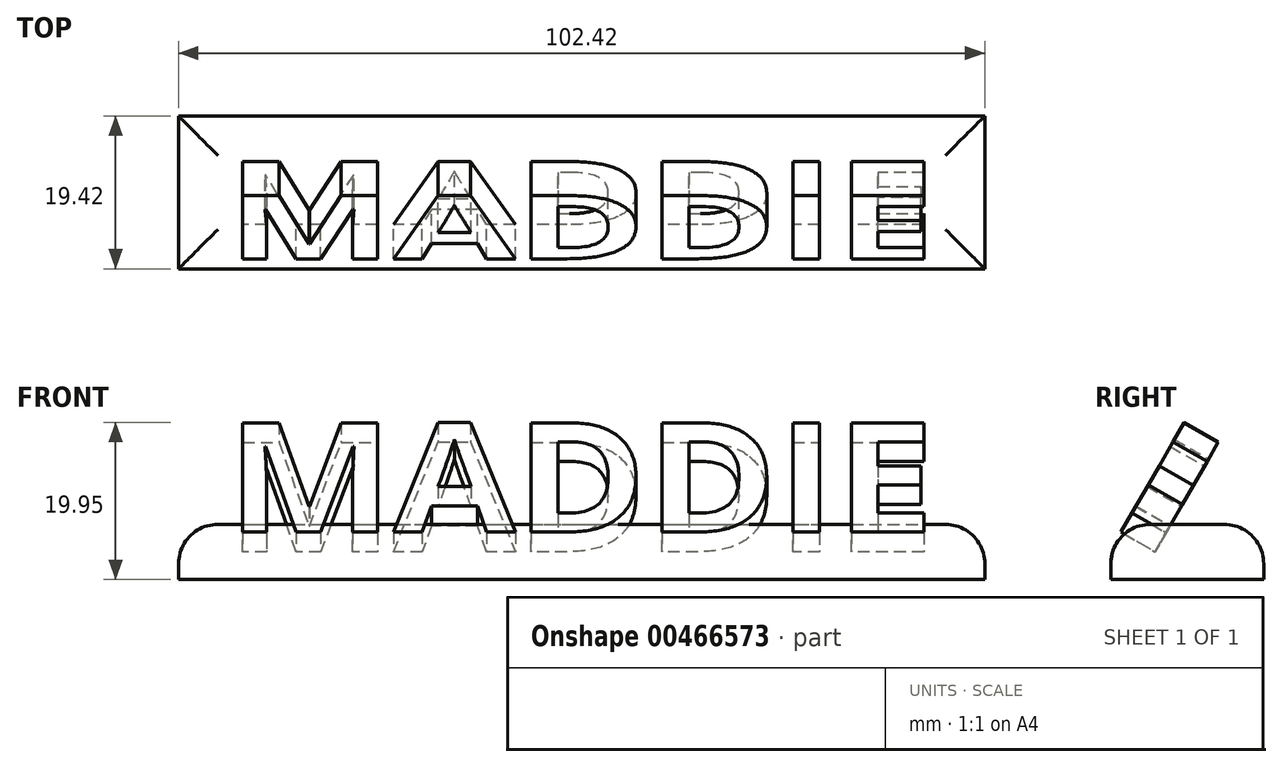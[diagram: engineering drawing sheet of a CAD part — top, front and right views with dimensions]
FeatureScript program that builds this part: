
annotation { "Feature Type Name" : "Feature", "Feature Type Description" : "" }
export const myFeature = defineFeature(function(context is Context, id is Id, definition is map)
    precondition{}
    {
        {
            var Q0;
            Q0=qCreatedBy(makeId("Top.planeOp"),FACE);
            var sketch = newSketch(context, id + "F0", { "sketchPlane" : qUnion([Q0])});
            skText(sketch, "E0", { "text": "MADDIE", "fontName": "OpenSans-Bold.ttf"});
            const initialGuessF0  = {"E0": [-0.03343, -0.00687, 1, 0, 0.01616]};
            skSetInitialGuess(sketch, initialGuessF0);
            skSolve(sketch);
        }
        {
            var Q0;
            Q0=qSketchRegion(id+"F0",true);
            extrude(context, id + "F1", {"entities" : qUnion([Q0]), "depth" : 5 * mm});
        }
        {
            var Q0;
            Q0=qCreatedBy(makeId("Top.planeOp"),FACE);
            var sketch = newSketch(context, id + "F2", { "sketchPlane" : qUnion([Q0])});
            skLineSegment(sketch, "E1.bottom", {"start": v(-39.57, 31.58) * mm, "end": v(62.85, 31.58) * mm});
            skLineSegment(sketch, "E1.top", {"start": v(-39.57, 12.16) * mm, "end": v(62.85, 12.16) * mm});
            skLineSegment(sketch, "E1.left", {"start": v(-39.57, 31.58) * mm, "end": v(-39.57, 12.16) * mm});
            skLineSegment(sketch, "E1.right", {"start": v(62.85, 31.58) * mm, "end": v(62.85, 12.16) * mm});
            skSolve(sketch);
        }
        {
            var Q0;
            Q0=makeQuery(id+"F2.imprint","IMPRINT",FACE,{"disambiguationData":[TD([[makeQuery(id+"F2.imprint","IMPRINT",EDGE,{"derivedFrom":sQuery(id+"F2.wireOp",EDGE,"E1.bottom")}),-1.0]])]});
            extrude(context, id + "F3", {"entities" : qUnion([Q0]), "depth" : 7 * mm});
        }
        {
            var Q0;
            Q0=makeQuery(id+"F3.opExtrude","CAP_EDGE",EDGE,{"disambiguationData":[OSD([sQuery(id+"F2.wireOp",EDGE,"E1.left")])],"isStart":false});
            var Q1;
            Q1=makeQuery(id+"F3.opExtrude","CAP_EDGE",EDGE,{"disambiguationData":[OSD([sQuery(id+"F2.wireOp",EDGE,"E1.top")])],"isStart":false});
            var Q2;
            Q2=makeQuery(id+"F3.opExtrude","CAP_EDGE",EDGE,{"disambiguationData":[OSD([sQuery(id+"F2.wireOp",EDGE,"E1.right")])],"isStart":false});
            var Q3;
            Q3=makeQuery(id+"F3.opExtrude","CAP_EDGE",EDGE,{"disambiguationData":[OSD([sQuery(id+"F2.wireOp",EDGE,"E1.bottom")])],"isStart":false});
            fillet(context, id + "F4", {"entities" : qUnion([Q0, Q1, Q2, Q3]), "radius" : 5 * mm, "tangentPropagation" : true, "allowEdgeOverflow" : false});
        }
        {
            var Q0;
            Q0=makeQuery(id+"F1.opExtrude","SWEPT_BODY",BODY,{"disambiguationData":[OSD([sQuery(id+"F0.wireOp",EDGE,"E0.sketch_text.stroke-46"),sQuery(id+"F0.wireOp",EDGE,"E0.sketch_text.stroke-47"),sQuery(id+"F0.wireOp",EDGE,"E0.sketch_text.stroke-48"),sQuery(id+"F0.wireOp",EDGE,"E0.sketch_text.stroke-49"),sQuery(id+"F0.wireOp",EDGE,"E0.sketch_text.stroke-50"),sQuery(id+"F0.wireOp",EDGE,"E0.sketch_text.stroke-51"),sQuery(id+"F0.wireOp",EDGE,"E0.sketch_text.stroke-52"),sQuery(id+"F0.wireOp",EDGE,"E0.sketch_text.stroke-53"),sQuery(id+"F0.wireOp",EDGE,"E0.sketch_text.stroke-54"),sQuery(id+"F0.wireOp",EDGE,"E0.sketch_text.stroke-55"),sQuery(id+"F0.wireOp",EDGE,"E0.sketch_text.stroke-56"),sQuery(id+"F0.wireOp",EDGE,"E0.sketch_text.stroke-57"),sQuery(id+"F0.wireOp",EDGE,"E0.sketch_text.stroke-58"),sQuery(id+"F0.wireOp",EDGE,"E0.sketch_text.stroke-59"),sQuery(id+"F0.wireOp",EDGE,"E0.sketch_text.stroke-60"),sQuery(id+"F0.wireOp",EDGE,"E0.sketch_text.stroke-61"),sQuery(id+"F0.wireOp",EDGE,"E0.sketch_text.stroke-62"),sQuery(id+"F0.wireOp",EDGE,"E0.sketch_text.stroke-63"),sQuery(id+"F0.wireOp",EDGE,"E0.sketch_text.stroke-64"),sQuery(id+"F0.wireOp",EDGE,"E0.sketch_text.stroke-65"),sQuery(id+"F0.wireOp",EDGE,"E0.sketch_text.stroke-66"),sQuery(id+"F0.wireOp",EDGE,"E0.sketch_text.stroke-67"),sQuery(id+"F0.wireOp",EDGE,"E0.sketch_text.stroke-68"),sQuery(id+"F0.wireOp",EDGE,"E0.sketch_text.stroke-69"),sQuery(id+"F0.wireOp",EDGE,"E0.sketch_text.stroke-70"),sQuery(id+"F0.wireOp",EDGE,"E0.sketch_text.stroke-71"),sQuery(id+"F0.wireOp",EDGE,"E0.sketch_text.stroke-72"),sQuery(id+"F0.wireOp",EDGE,"E0.sketch_text.stroke-73")])]});
            var Q1;
            Q1=makeQuery(id+"F1.opExtrude","SWEPT_BODY",BODY,{"disambiguationData":[OSD([sQuery(id+"F0.wireOp",EDGE,"E0.sketch_text.stroke-55"),sQuery(id+"F0.wireOp",EDGE,"E0.sketch_text.stroke-56"),sQuery(id+"F0.wireOp",EDGE,"E0.sketch_text.stroke-57"),sQuery(id+"F0.wireOp",EDGE,"E0.sketch_text.stroke-58")])]});
            var Q2;
            Q2=makeQuery(id+"F1.opExtrude","SWEPT_BODY",BODY,{"disambiguationData":[OSD([sQuery(id+"F0.wireOp",EDGE,"E0.sketch_text.stroke-31"),sQuery(id+"F0.wireOp",EDGE,"E0.sketch_text.stroke-32"),sQuery(id+"F0.wireOp",EDGE,"E0.sketch_text.stroke-33"),sQuery(id+"F0.wireOp",EDGE,"E0.sketch_text.stroke-34"),sQuery(id+"F0.wireOp",EDGE,"E0.sketch_text.stroke-35"),sQuery(id+"F0.wireOp",EDGE,"E0.sketch_text.stroke-36"),sQuery(id+"F0.wireOp",EDGE,"E0.sketch_text.stroke-37"),sQuery(id+"F0.wireOp",EDGE,"E0.sketch_text.stroke-38"),sQuery(id+"F0.wireOp",EDGE,"E0.sketch_text.stroke-39"),sQuery(id+"F0.wireOp",EDGE,"E0.sketch_text.stroke-40"),sQuery(id+"F0.wireOp",EDGE,"E0.sketch_text.stroke-41"),sQuery(id+"F0.wireOp",EDGE,"E0.sketch_text.stroke-42")])]});
            var Q3;
            Q3=makeQuery(id+"F1.opExtrude","SWEPT_BODY",BODY,{"disambiguationData":[OSD([sQuery(id+"F0.wireOp",EDGE,"E0.sketch_text.stroke-43"),sQuery(id+"F0.wireOp",EDGE,"E0.sketch_text.stroke-44"),sQuery(id+"F0.wireOp",EDGE,"E0.sketch_text.stroke-45"),sQuery(id+"F0.wireOp",EDGE,"E0.sketch_text.stroke-46"),sQuery(id+"F0.wireOp",EDGE,"E0.sketch_text.stroke-47"),sQuery(id+"F0.wireOp",EDGE,"E0.sketch_text.stroke-48"),sQuery(id+"F0.wireOp",EDGE,"E0.sketch_text.stroke-49"),sQuery(id+"F0.wireOp",EDGE,"E0.sketch_text.stroke-50"),sQuery(id+"F0.wireOp",EDGE,"E0.sketch_text.stroke-51"),sQuery(id+"F0.wireOp",EDGE,"E0.sketch_text.stroke-52"),sQuery(id+"F0.wireOp",EDGE,"E0.sketch_text.stroke-53"),sQuery(id+"F0.wireOp",EDGE,"E0.sketch_text.stroke-54")])]});
            var Q4;
            Q4=makeQuery(id+"F1.opExtrude","SWEPT_BODY",BODY,{"disambiguationData":[OSD([sQuery(id+"F0.wireOp",EDGE,"E0.sketch_text.stroke-19"),sQuery(id+"F0.wireOp",EDGE,"E0.sketch_text.stroke-20"),sQuery(id+"F0.wireOp",EDGE,"E0.sketch_text.stroke-21"),sQuery(id+"F0.wireOp",EDGE,"E0.sketch_text.stroke-22"),sQuery(id+"F0.wireOp",EDGE,"E0.sketch_text.stroke-23"),sQuery(id+"F0.wireOp",EDGE,"E0.sketch_text.stroke-24"),sQuery(id+"F0.wireOp",EDGE,"E0.sketch_text.stroke-25"),sQuery(id+"F0.wireOp",EDGE,"E0.sketch_text.stroke-26"),sQuery(id+"F0.wireOp",EDGE,"E0.sketch_text.stroke-27"),sQuery(id+"F0.wireOp",EDGE,"E0.sketch_text.stroke-28"),sQuery(id+"F0.wireOp",EDGE,"E0.sketch_text.stroke-29"),sQuery(id+"F0.wireOp",EDGE,"E0.sketch_text.stroke-30")])]});
            var Q5;
            Q5=makeQuery(id+"F1.opExtrude","SWEPT_BODY",BODY,{"disambiguationData":[OSD([sQuery(id+"F0.wireOp",EDGE,"E0.sketch_text.stroke-0"),sQuery(id+"F0.wireOp",EDGE,"E0.sketch_text.stroke-1"),sQuery(id+"F0.wireOp",EDGE,"E0.sketch_text.stroke-2"),sQuery(id+"F0.wireOp",EDGE,"E0.sketch_text.stroke-3"),sQuery(id+"F0.wireOp",EDGE,"E0.sketch_text.stroke-4"),sQuery(id+"F0.wireOp",EDGE,"E0.sketch_text.stroke-5"),sQuery(id+"F0.wireOp",EDGE,"E0.sketch_text.stroke-6"),sQuery(id+"F0.wireOp",EDGE,"E0.sketch_text.stroke-7"),sQuery(id+"F0.wireOp",EDGE,"E0.sketch_text.stroke-8"),sQuery(id+"F0.wireOp",EDGE,"E0.sketch_text.stroke-9"),sQuery(id+"F0.wireOp",EDGE,"E0.sketch_text.stroke-10"),sQuery(id+"F0.wireOp",EDGE,"E0.sketch_text.stroke-11"),sQuery(id+"F0.wireOp",EDGE,"E0.sketch_text.stroke-12"),sQuery(id+"F0.wireOp",EDGE,"E0.sketch_text.stroke-13"),sQuery(id+"F0.wireOp",EDGE,"E0.sketch_text.stroke-14"),sQuery(id+"F0.wireOp",EDGE,"E0.sketch_text.stroke-15"),sQuery(id+"F0.wireOp",EDGE,"E0.sketch_text.stroke-16"),sQuery(id+"F0.wireOp",EDGE,"E0.sketch_text.stroke-17"),sQuery(id+"F0.wireOp",EDGE,"E0.sketch_text.stroke-18")])]});
            var Q6;
            Q6=makeQuery(id+"F1.opExtrude","CAP_EDGE",EDGE,{"disambiguationData":[OSD([sQuery(id+"F0.wireOp",EDGE,"E0.sketch_text.stroke-26")])],"isStart":false});
            transform(context, id + "F5", {"entities" : qUnion([Q0, Q1, Q2, Q3, Q4, Q5]), "transformType" : TransformType.ROTATION, "transformAxis" : qUnion([Q6]), "angle" : 60 * degree, "oppositeDirection" : true, "makeCopy" : false});
        }
        {
            var Q0;
            Q0=makeQuery(id+"F1.opExtrude","SWEPT_BODY",BODY,{"disambiguationData":[OSD([sQuery(id+"F0.wireOp",EDGE,"E0.sketch_text.stroke-59"),sQuery(id+"F0.wireOp",EDGE,"E0.sketch_text.stroke-60"),sQuery(id+"F0.wireOp",EDGE,"E0.sketch_text.stroke-61"),sQuery(id+"F0.wireOp",EDGE,"E0.sketch_text.stroke-62"),sQuery(id+"F0.wireOp",EDGE,"E0.sketch_text.stroke-63"),sQuery(id+"F0.wireOp",EDGE,"E0.sketch_text.stroke-64"),sQuery(id+"F0.wireOp",EDGE,"E0.sketch_text.stroke-65"),sQuery(id+"F0.wireOp",EDGE,"E0.sketch_text.stroke-66"),sQuery(id+"F0.wireOp",EDGE,"E0.sketch_text.stroke-67"),sQuery(id+"F0.wireOp",EDGE,"E0.sketch_text.stroke-68"),sQuery(id+"F0.wireOp",EDGE,"E0.sketch_text.stroke-69"),sQuery(id+"F0.wireOp",EDGE,"E0.sketch_text.stroke-70")])]});
            var Q1;
            Q1=makeQuery(id+"F1.opExtrude","SWEPT_BODY",BODY,{"disambiguationData":[OSD([sQuery(id+"F0.wireOp",EDGE,"E0.sketch_text.stroke-55"),sQuery(id+"F0.wireOp",EDGE,"E0.sketch_text.stroke-56"),sQuery(id+"F0.wireOp",EDGE,"E0.sketch_text.stroke-57"),sQuery(id+"F0.wireOp",EDGE,"E0.sketch_text.stroke-58")])]});
            var Q2;
            Q2=makeQuery(id+"F1.opExtrude","SWEPT_BODY",BODY,{"disambiguationData":[OSD([sQuery(id+"F0.wireOp",EDGE,"E0.sketch_text.stroke-43"),sQuery(id+"F0.wireOp",EDGE,"E0.sketch_text.stroke-44"),sQuery(id+"F0.wireOp",EDGE,"E0.sketch_text.stroke-45"),sQuery(id+"F0.wireOp",EDGE,"E0.sketch_text.stroke-46"),sQuery(id+"F0.wireOp",EDGE,"E0.sketch_text.stroke-47"),sQuery(id+"F0.wireOp",EDGE,"E0.sketch_text.stroke-48"),sQuery(id+"F0.wireOp",EDGE,"E0.sketch_text.stroke-49"),sQuery(id+"F0.wireOp",EDGE,"E0.sketch_text.stroke-50"),sQuery(id+"F0.wireOp",EDGE,"E0.sketch_text.stroke-51"),sQuery(id+"F0.wireOp",EDGE,"E0.sketch_text.stroke-52"),sQuery(id+"F0.wireOp",EDGE,"E0.sketch_text.stroke-53"),sQuery(id+"F0.wireOp",EDGE,"E0.sketch_text.stroke-54")])]});
            var Q3;
            Q3=makeQuery(id+"F1.opExtrude","SWEPT_BODY",BODY,{"disambiguationData":[OSD([sQuery(id+"F0.wireOp",EDGE,"E0.sketch_text.stroke-31"),sQuery(id+"F0.wireOp",EDGE,"E0.sketch_text.stroke-32"),sQuery(id+"F0.wireOp",EDGE,"E0.sketch_text.stroke-33"),sQuery(id+"F0.wireOp",EDGE,"E0.sketch_text.stroke-34"),sQuery(id+"F0.wireOp",EDGE,"E0.sketch_text.stroke-35"),sQuery(id+"F0.wireOp",EDGE,"E0.sketch_text.stroke-36"),sQuery(id+"F0.wireOp",EDGE,"E0.sketch_text.stroke-37"),sQuery(id+"F0.wireOp",EDGE,"E0.sketch_text.stroke-38"),sQuery(id+"F0.wireOp",EDGE,"E0.sketch_text.stroke-39"),sQuery(id+"F0.wireOp",EDGE,"E0.sketch_text.stroke-40"),sQuery(id+"F0.wireOp",EDGE,"E0.sketch_text.stroke-41"),sQuery(id+"F0.wireOp",EDGE,"E0.sketch_text.stroke-42")])]});
            var Q4;
            Q4=makeQuery(id+"F1.opExtrude","SWEPT_BODY",BODY,{"disambiguationData":[OSD([sQuery(id+"F0.wireOp",EDGE,"E0.sketch_text.stroke-19"),sQuery(id+"F0.wireOp",EDGE,"E0.sketch_text.stroke-20"),sQuery(id+"F0.wireOp",EDGE,"E0.sketch_text.stroke-21"),sQuery(id+"F0.wireOp",EDGE,"E0.sketch_text.stroke-22"),sQuery(id+"F0.wireOp",EDGE,"E0.sketch_text.stroke-23"),sQuery(id+"F0.wireOp",EDGE,"E0.sketch_text.stroke-24"),sQuery(id+"F0.wireOp",EDGE,"E0.sketch_text.stroke-25"),sQuery(id+"F0.wireOp",EDGE,"E0.sketch_text.stroke-26"),sQuery(id+"F0.wireOp",EDGE,"E0.sketch_text.stroke-27"),sQuery(id+"F0.wireOp",EDGE,"E0.sketch_text.stroke-28"),sQuery(id+"F0.wireOp",EDGE,"E0.sketch_text.stroke-29"),sQuery(id+"F0.wireOp",EDGE,"E0.sketch_text.stroke-30")])]});
            var Q5;
            Q5=makeQuery(id+"F1.opExtrude","SWEPT_BODY",BODY,{"disambiguationData":[OSD([sQuery(id+"F0.wireOp",EDGE,"E0.sketch_text.stroke-0"),sQuery(id+"F0.wireOp",EDGE,"E0.sketch_text.stroke-1"),sQuery(id+"F0.wireOp",EDGE,"E0.sketch_text.stroke-2"),sQuery(id+"F0.wireOp",EDGE,"E0.sketch_text.stroke-3"),sQuery(id+"F0.wireOp",EDGE,"E0.sketch_text.stroke-4"),sQuery(id+"F0.wireOp",EDGE,"E0.sketch_text.stroke-5"),sQuery(id+"F0.wireOp",EDGE,"E0.sketch_text.stroke-6"),sQuery(id+"F0.wireOp",EDGE,"E0.sketch_text.stroke-7"),sQuery(id+"F0.wireOp",EDGE,"E0.sketch_text.stroke-8"),sQuery(id+"F0.wireOp",EDGE,"E0.sketch_text.stroke-9"),sQuery(id+"F0.wireOp",EDGE,"E0.sketch_text.stroke-10"),sQuery(id+"F0.wireOp",EDGE,"E0.sketch_text.stroke-11"),sQuery(id+"F0.wireOp",EDGE,"E0.sketch_text.stroke-12"),sQuery(id+"F0.wireOp",EDGE,"E0.sketch_text.stroke-13"),sQuery(id+"F0.wireOp",EDGE,"E0.sketch_text.stroke-14"),sQuery(id+"F0.wireOp",EDGE,"E0.sketch_text.stroke-15"),sQuery(id+"F0.wireOp",EDGE,"E0.sketch_text.stroke-16"),sQuery(id+"F0.wireOp",EDGE,"E0.sketch_text.stroke-17"),sQuery(id+"F0.wireOp",EDGE,"E0.sketch_text.stroke-18")])]});
            transform(context, id + "F6", {"entities" : qUnion([Q0, Q1, Q2, Q3, Q4, Q5]), "transformType" : TransformType.TRANSLATION_3D, "dx" : 0 * mm, "dy" : 20.32 * mm, "dz" : 1.02 * mm, "makeCopy" : false});
        }
    });
